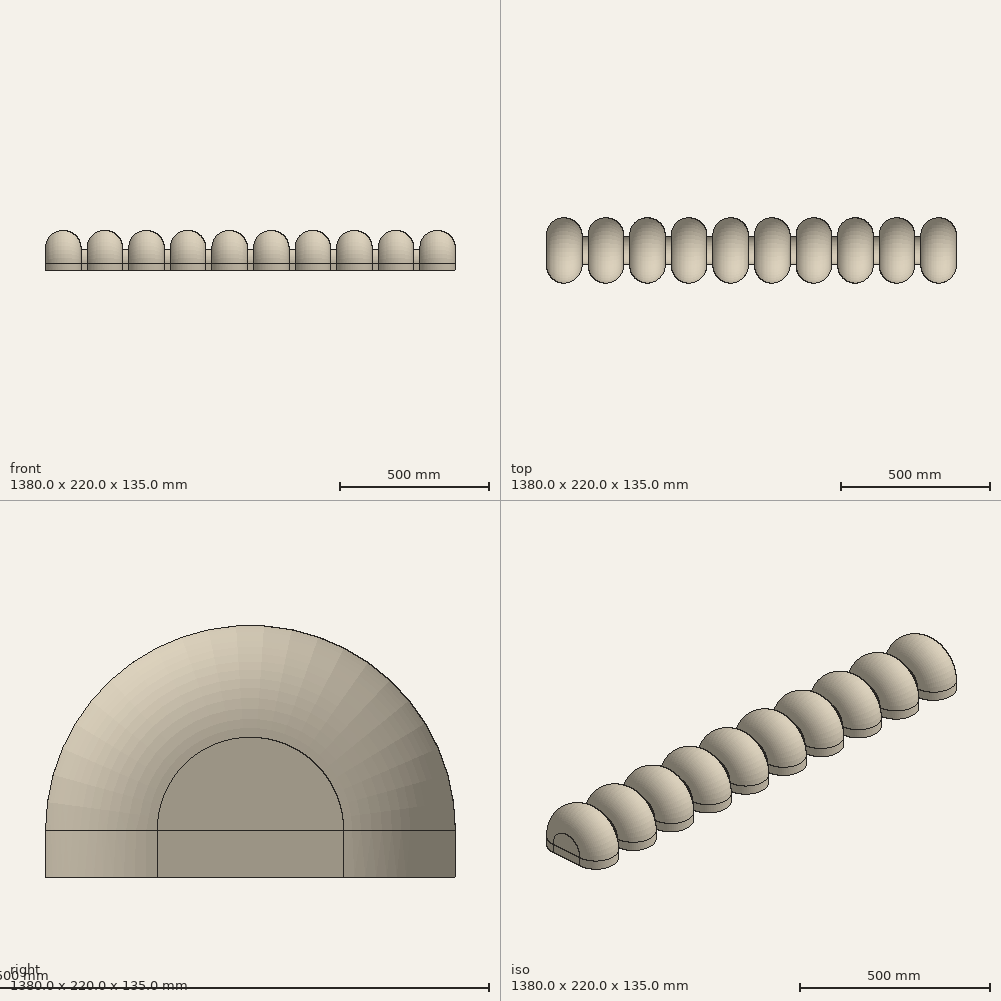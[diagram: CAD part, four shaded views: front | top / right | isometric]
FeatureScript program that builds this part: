
annotation { "Feature Type Name" : "Feature", "Feature Type Description" : "" }
export const myFeature = defineFeature(function(context is Context, id is Id, definition is map)
    precondition{}
    {
        {
            var Q0;
            Q0=qCreatedBy(makeId("Top.planeOp"),FACE);
            var sketch = newSketch(context, id + "F0", { "sketchPlane" : qUnion([Q0])});
            skArc(sketch, "E0", {"start": v(50, 0) * mm, "mid": v(0, 50) * mm, "end": v(-50, 0) * mm});
            skLineSegment(sketch, "E1", {"start": v(-50, 0) * mm, "end": v(-50, -100) * mm});
            skLineSegment(sketch, "E2", {"start": v(50, 0) * mm, "end": v(50, -13) * mm});
            skArc(sketch, "E3", {"start": v(-50, -100) * mm, "mid": v(0, -150) * mm, "end": v(50, -100) * mm});
            skLineSegment(sketch, "E4.bottom", {"start": v(50, -13) * mm, "end": v(90, -13) * mm});
            skLineSegment(sketch, "E4.top", {"start": v(50, -87) * mm, "end": v(90, -87) * mm});
            skLineSegment(sketch, "E5", {"start": v(90, 0) * mm, "end": v(90, -13) * mm});
            skLineSegment(sketch, "E6", {"start": v(190, 0) * mm, "end": v(190, -13) * mm});
            skArc(sketch, "E7", {"start": v(90, 0) * mm, "mid": v(140, 50) * mm, "end": v(190, 0) * mm});
            skArc(sketch, "E8", {"start": v(190, -100) * mm, "mid": v(140, -150) * mm, "end": v(90, -100) * mm});
            skLineSegment(sketch, "E9.trimOffspring", {"start": v(90, -87) * mm, "end": v(90, -100) * mm});
            skLineSegment(sketch, "E10.trimOffspring", {"start": v(50, -87) * mm, "end": v(50, -100) * mm});
            skLineSegment(sketch, "E11.bottom", {"start": v(190, -13) * mm, "end": v(230, -13) * mm});
            skLineSegment(sketch, "E11.top", {"start": v(190, -87) * mm, "end": v(230, -87) * mm});
            skLineSegment(sketch, "E12", {"start": v(230, 0) * mm, "end": v(230, -13) * mm});
            skLineSegment(sketch, "E13", {"start": v(330, -100) * mm, "end": v(330, -87) * mm});
            skArc(sketch, "E14", {"start": v(230, 0) * mm, "mid": v(280, 50) * mm, "end": v(330, 0) * mm});
            skArc(sketch, "E15", {"start": v(330, -100) * mm, "mid": v(280, -150) * mm, "end": v(230, -100) * mm});
            skLineSegment(sketch, "E16.trimOffspring", {"start": v(190, -87) * mm, "end": v(190, -100) * mm});
            skLineSegment(sketch, "E17.trimOffspring", {"start": v(230, -87) * mm, "end": v(230, -100) * mm});
            skLineSegment(sketch, "E18.bottom", {"start": v(330, -13) * mm, "end": v(370, -13) * mm});
            skLineSegment(sketch, "E18.top", {"start": v(330, -87) * mm, "end": v(370, -87) * mm});
            skLineSegment(sketch, "E19", {"start": v(370, 0) * mm, "end": v(370, -13) * mm});
            skLineSegment(sketch, "E20", {"start": v(470, -100) * mm, "end": v(470, -87) * mm});
            skArc(sketch, "E21", {"start": v(370, 0) * mm, "mid": v(420, 50) * mm, "end": v(470, 0) * mm});
            skArc(sketch, "E22", {"start": v(470, -100) * mm, "mid": v(420, -150) * mm, "end": v(370, -100) * mm});
            skLineSegment(sketch, "E23.bottom", {"start": v(470, -13) * mm, "end": v(510, -13) * mm});
            skLineSegment(sketch, "E23.top", {"start": v(470, -87) * mm, "end": v(510, -87) * mm});
            skLineSegment(sketch, "E24", {"start": v(510, 0) * mm, "end": v(510, -13) * mm});
            skLineSegment(sketch, "E25", {"start": v(610, -100) * mm, "end": v(610, -87) * mm});
            skArc(sketch, "E26", {"start": v(510, 0) * mm, "mid": v(560, 50) * mm, "end": v(610, 0) * mm});
            skArc(sketch, "E27", {"start": v(610, -100) * mm, "mid": v(560, -150) * mm, "end": v(510, -100) * mm});
            skLineSegment(sketch, "E28.bottom", {"start": v(610, -13) * mm, "end": v(650, -13) * mm});
            skLineSegment(sketch, "E28.top", {"start": v(610, -87) * mm, "end": v(650, -87) * mm});
            skLineSegment(sketch, "E29", {"start": v(650, 0) * mm, "end": v(650, -13) * mm});
            skLineSegment(sketch, "E30", {"start": v(750, -100) * mm, "end": v(750, -87) * mm});
            skArc(sketch, "E31", {"start": v(650, 0) * mm, "mid": v(700, 50) * mm, "end": v(750, 0) * mm});
            skArc(sketch, "E32", {"start": v(750, -100) * mm, "mid": v(700, -150) * mm, "end": v(650, -100) * mm});
            skLineSegment(sketch, "E33.bottom", {"start": v(750, -13) * mm, "end": v(790, -13) * mm});
            skLineSegment(sketch, "E33.top", {"start": v(750, -87) * mm, "end": v(790, -87) * mm});
            skLineSegment(sketch, "E34", {"start": v(790, 0) * mm, "end": v(790, -13) * mm});
            skLineSegment(sketch, "E35", {"start": v(890, -100) * mm, "end": v(890, -87) * mm});
            skArc(sketch, "E36", {"start": v(790, 0) * mm, "mid": v(840, 50) * mm, "end": v(890, 0) * mm});
            skArc(sketch, "E37", {"start": v(890, -100) * mm, "mid": v(840, -150) * mm, "end": v(790, -100) * mm});
            skLineSegment(sketch, "E38.bottom", {"start": v(890, -13) * mm, "end": v(930, -13) * mm});
            skLineSegment(sketch, "E38.top", {"start": v(890, -87) * mm, "end": v(930, -87) * mm});
            skLineSegment(sketch, "E39", {"start": v(930, 0) * mm, "end": v(930, -13) * mm});
            skLineSegment(sketch, "E40", {"start": v(1030, -100) * mm, "end": v(1030, -87) * mm});
            skArc(sketch, "E41", {"start": v(1030, 0) * mm, "mid": v(980, 50) * mm, "end": v(930, 0) * mm});
            skArc(sketch, "E42", {"start": v(930, -100) * mm, "mid": v(980, -150) * mm, "end": v(1030, -100) * mm});
            skLineSegment(sketch, "E43.bottom", {"start": v(1030, -13) * mm, "end": v(1070, -13) * mm});
            skLineSegment(sketch, "E43.top", {"start": v(1030, -87) * mm, "end": v(1070, -87) * mm});
            skLineSegment(sketch, "E44", {"start": v(1070, 0) * mm, "end": v(1070, -13) * mm});
            skLineSegment(sketch, "E45", {"start": v(1170, -100) * mm, "end": v(1170, -87) * mm});
            skArc(sketch, "E46", {"start": v(1170, 0) * mm, "mid": v(1120, 50) * mm, "end": v(1070, 0) * mm});
            skArc(sketch, "E47", {"start": v(1070, -100) * mm, "mid": v(1120, -150) * mm, "end": v(1170, -100) * mm});
            skLineSegment(sketch, "E48.bottom", {"start": v(1170, -13) * mm, "end": v(1210, -13) * mm});
            skLineSegment(sketch, "E48.top", {"start": v(1170, -87) * mm, "end": v(1210, -87) * mm});
            skLineSegment(sketch, "E49", {"start": v(1210, 0) * mm, "end": v(1210, -13) * mm});
            skLineSegment(sketch, "E50", {"start": v(1310, -100) * mm, "end": v(1310, 0) * mm});
            skArc(sketch, "E51", {"start": v(1310, 0) * mm, "mid": v(1260, 50) * mm, "end": v(1210, 0) * mm});
            skArc(sketch, "E52", {"start": v(1310, -100) * mm, "mid": v(1260, -150) * mm, "end": v(1210, -100) * mm});
            skLineSegment(sketch, "E53.trimOffspring", {"start": v(1170, -13) * mm, "end": v(1170, 0) * mm});
            skLineSegment(sketch, "E54.trimOffspring", {"start": v(1210, -87) * mm, "end": v(1210, -100) * mm});
            skLineSegment(sketch, "E55.trimOffspring", {"start": v(1030, -13) * mm, "end": v(1030, 0) * mm});
            skLineSegment(sketch, "E56.trimOffspring", {"start": v(1070, -87) * mm, "end": v(1070, -100) * mm});
            skLineSegment(sketch, "E57.trimOffspring", {"start": v(930, -87) * mm, "end": v(930, -100) * mm});
            skLineSegment(sketch, "E58.trimOffspring", {"start": v(890, -13) * mm, "end": v(890, 0) * mm});
            skLineSegment(sketch, "E59.trimOffspring", {"start": v(790, -87) * mm, "end": v(790, -100) * mm});
            skLineSegment(sketch, "E60.trimOffspring", {"start": v(750, -13) * mm, "end": v(750, 0) * mm});
            skLineSegment(sketch, "E61.trimOffspring", {"start": v(650, -87) * mm, "end": v(650, -100) * mm});
            skLineSegment(sketch, "E62.trimOffspring", {"start": v(610, -13) * mm, "end": v(610, 0) * mm});
            skLineSegment(sketch, "E63.trimOffspring", {"start": v(510, -87) * mm, "end": v(510, -100) * mm});
            skLineSegment(sketch, "E64.trimOffspring", {"start": v(470, -13) * mm, "end": v(470, 0) * mm});
            skLineSegment(sketch, "E65.trimOffspring", {"start": v(370, -87) * mm, "end": v(370, -100) * mm});
            skLineSegment(sketch, "E66.trimOffspring", {"start": v(330, -13) * mm, "end": v(330, 0) * mm});
            skSolve(sketch);
        }
        {
            var Q0;
            Q0=makeQuery(id+"F0.imprint","IMPRINT",FACE,{"disambiguationData":[TD([[makeQuery(id+"F0.imprint","IMPRINT",EDGE,{"derivedFrom":sQuery(id+"F0.wireOp",EDGE,"E0")}),1.0]])]});
            extrude(context, id + "F1", {"entities" : qUnion([Q0]), "depth" : 25 * mm});
        }
        {
            var Q0;
            Q0=makeQuery(id+"F1.opExtrude","CAP_FACE",FACE,{"disambiguationData":[OSD([sQuery(id+"F0.wireOp",EDGE,"E0"),sQuery(id+"F0.wireOp",EDGE,"E1"),sQuery(id+"F0.wireOp",EDGE,"E2"),sQuery(id+"F0.wireOp",EDGE,"E3"),sQuery(id+"F0.wireOp",EDGE,"E4.bottom"),sQuery(id+"F0.wireOp",EDGE,"E4.top"),sQuery(id+"F0.wireOp",EDGE,"E5"),sQuery(id+"F0.wireOp",EDGE,"E6"),sQuery(id+"F0.wireOp",EDGE,"E7"),sQuery(id+"F0.wireOp",EDGE,"E8"),sQuery(id+"F0.wireOp",EDGE,"E9.trimOffspring"),sQuery(id+"F0.wireOp",EDGE,"E10.trimOffspring"),sQuery(id+"F0.wireOp",EDGE,"E11.bottom"),sQuery(id+"F0.wireOp",EDGE,"E11.top"),sQuery(id+"F0.wireOp",EDGE,"E12"),sQuery(id+"F0.wireOp",EDGE,"E13"),sQuery(id+"F0.wireOp",EDGE,"E14"),sQuery(id+"F0.wireOp",EDGE,"E15"),sQuery(id+"F0.wireOp",EDGE,"E16.trimOffspring"),sQuery(id+"F0.wireOp",EDGE,"E17.trimOffspring"),sQuery(id+"F0.wireOp",EDGE,"E18.bottom"),sQuery(id+"F0.wireOp",EDGE,"E18.top"),sQuery(id+"F0.wireOp",EDGE,"E19"),sQuery(id+"F0.wireOp",EDGE,"E20"),sQuery(id+"F0.wireOp",EDGE,"E21"),sQuery(id+"F0.wireOp",EDGE,"E22"),sQuery(id+"F0.wireOp",EDGE,"E23.bottom"),sQuery(id+"F0.wireOp",EDGE,"E23.top"),sQuery(id+"F0.wireOp",EDGE,"E24"),sQuery(id+"F0.wireOp",EDGE,"E25"),sQuery(id+"F0.wireOp",EDGE,"E26"),sQuery(id+"F0.wireOp",EDGE,"E27"),sQuery(id+"F0.wireOp",EDGE,"E28.bottom"),sQuery(id+"F0.wireOp",EDGE,"E28.top"),sQuery(id+"F0.wireOp",EDGE,"E29"),sQuery(id+"F0.wireOp",EDGE,"E30"),sQuery(id+"F0.wireOp",EDGE,"E31"),sQuery(id+"F0.wireOp",EDGE,"E32"),sQuery(id+"F0.wireOp",EDGE,"E33.bottom"),sQuery(id+"F0.wireOp",EDGE,"E33.top"),sQuery(id+"F0.wireOp",EDGE,"E34"),sQuery(id+"F0.wireOp",EDGE,"E35"),sQuery(id+"F0.wireOp",EDGE,"E36"),sQuery(id+"F0.wireOp",EDGE,"E37"),sQuery(id+"F0.wireOp",EDGE,"E38.bottom"),sQuery(id+"F0.wireOp",EDGE,"E38.top"),sQuery(id+"F0.wireOp",EDGE,"E39"),sQuery(id+"F0.wireOp",EDGE,"E40"),sQuery(id+"F0.wireOp",EDGE,"E41"),sQuery(id+"F0.wireOp",EDGE,"E42"),sQuery(id+"F0.wireOp",EDGE,"E43.bottom"),sQuery(id+"F0.wireOp",EDGE,"E43.top"),sQuery(id+"F0.wireOp",EDGE,"E44"),sQuery(id+"F0.wireOp",EDGE,"E45"),sQuery(id+"F0.wireOp",EDGE,"E46"),sQuery(id+"F0.wireOp",EDGE,"E47"),sQuery(id+"F0.wireOp",EDGE,"E48.bottom"),sQuery(id+"F0.wireOp",EDGE,"E48.top"),sQuery(id+"F0.wireOp",EDGE,"E49"),sQuery(id+"F0.wireOp",EDGE,"E50"),sQuery(id+"F0.wireOp",EDGE,"E51"),sQuery(id+"F0.wireOp",EDGE,"E52"),sQuery(id+"F0.wireOp",EDGE,"E53.trimOffspring"),sQuery(id+"F0.wireOp",EDGE,"E54.trimOffspring"),sQuery(id+"F0.wireOp",EDGE,"E55.trimOffspring"),sQuery(id+"F0.wireOp",EDGE,"E56.trimOffspring"),sQuery(id+"F0.wireOp",EDGE,"E57.trimOffspring"),sQuery(id+"F0.wireOp",EDGE,"E58.trimOffspring"),sQuery(id+"F0.wireOp",EDGE,"E59.trimOffspring"),sQuery(id+"F0.wireOp",EDGE,"E60.trimOffspring"),sQuery(id+"F0.wireOp",EDGE,"E61.trimOffspring"),sQuery(id+"F0.wireOp",EDGE,"E62.trimOffspring"),sQuery(id+"F0.wireOp",EDGE,"E63.trimOffspring"),sQuery(id+"F0.wireOp",EDGE,"E64.trimOffspring"),sQuery(id+"F0.wireOp",EDGE,"E65.trimOffspring"),sQuery(id+"F0.wireOp",EDGE,"E66.trimOffspring")])],"isStart":false});
            var sketch = newSketch(context, id + "F2", { "sketchPlane" : qUnion([Q0])});
            skLineSegment(sketch, "E67", {"start": v(470, 0) * mm, "end": v(470, -13) * mm});
            skLineSegment(sketch, "E68", {"start": v(470, -13) * mm, "end": v(510, -13) * mm});
            skLineSegment(sketch, "E69", {"start": v(510, -13) * mm, "end": v(510, 0) * mm});
            skArc(sketch, "E70", {"start": v(510, 0) * mm, "mid": v(560, 50) * mm, "end": v(610, 0) * mm});
            skLineSegment(sketch, "E71", {"start": v(610, 0) * mm, "end": v(610, -13) * mm});
            skLineSegment(sketch, "E72", {"start": v(610, -13) * mm, "end": v(650, -13) * mm});
            skLineSegment(sketch, "E73", {"start": v(650, -13) * mm, "end": v(650, 0) * mm});
            skArc(sketch, "E74", {"start": v(650, 0) * mm, "mid": v(700, 50) * mm, "end": v(750, 0) * mm});
            skLineSegment(sketch, "E75", {"start": v(750, 0) * mm, "end": v(750, -13) * mm});
            skLineSegment(sketch, "E76", {"start": v(750, -13) * mm, "end": v(790, -13) * mm});
            skLineSegment(sketch, "E77", {"start": v(790, -13) * mm, "end": v(790, 0) * mm});
            skArc(sketch, "E78", {"start": v(790, 0) * mm, "mid": v(840, 50) * mm, "end": v(890, 0) * mm});
            skLineSegment(sketch, "E79", {"start": v(890, 0) * mm, "end": v(890, -13) * mm});
            skLineSegment(sketch, "E80", {"start": v(890, -13) * mm, "end": v(930, -13) * mm});
            skLineSegment(sketch, "E81", {"start": v(930, -13) * mm, "end": v(930, 0) * mm});
            skArc(sketch, "E82", {"start": v(930, 0) * mm, "mid": v(980, 50) * mm, "end": v(1030, 0) * mm});
            skLineSegment(sketch, "E83", {"start": v(1030, 0) * mm, "end": v(1030, -13) * mm});
            skLineSegment(sketch, "E84", {"start": v(1030, -13) * mm, "end": v(1070, -13) * mm});
            skLineSegment(sketch, "E85", {"start": v(1070, -13) * mm, "end": v(1070, 0) * mm});
            skArc(sketch, "E86", {"start": v(1070, 0) * mm, "mid": v(1120, 50) * mm, "end": v(1170, 0) * mm});
            skLineSegment(sketch, "E87", {"start": v(1170, 0) * mm, "end": v(1170, -13) * mm});
            skLineSegment(sketch, "E88", {"start": v(1170, -13) * mm, "end": v(1210, -13) * mm});
            skLineSegment(sketch, "E89", {"start": v(1210, -13) * mm, "end": v(1210, 0) * mm});
            skArc(sketch, "E90", {"start": v(1210, 0) * mm, "mid": v(1260, 50) * mm, "end": v(1310, 0) * mm});
            skLineSegment(sketch, "E91", {"start": v(1310, 0) * mm, "end": v(1310, -50) * mm});
            skLineSegment(sketch, "E92", {"start": v(330, 0) * mm, "end": v(330, -13) * mm});
            skLineSegment(sketch, "E93", {"start": v(330, -13) * mm, "end": v(370, -13) * mm});
            skLineSegment(sketch, "E94", {"start": v(370, -13) * mm, "end": v(370, 0) * mm});
            skArc(sketch, "E95", {"start": v(470, 0) * mm, "mid": v(420, 50) * mm, "end": v(370, 0) * mm});
            skArc(sketch, "E96", {"start": v(330, 0) * mm, "mid": v(280, 50) * mm, "end": v(230, 0) * mm});
            skLineSegment(sketch, "E97", {"start": v(230, 0) * mm, "end": v(230, -13) * mm});
            skLineSegment(sketch, "E98", {"start": v(230, -13) * mm, "end": v(190, -13) * mm});
            skLineSegment(sketch, "E99", {"start": v(190, -13) * mm, "end": v(190, 0) * mm});
            skArc(sketch, "E100", {"start": v(190, 0) * mm, "mid": v(140, 50) * mm, "end": v(90, 0) * mm});
            skLineSegment(sketch, "E101", {"start": v(90, 0) * mm, "end": v(90, -13) * mm});
            skLineSegment(sketch, "E102", {"start": v(90, -13) * mm, "end": v(50, -13) * mm});
            skLineSegment(sketch, "E103", {"start": v(50, -13) * mm, "end": v(50, 0) * mm});
            skArc(sketch, "E104", {"start": v(50, 0) * mm, "mid": v(0, 50) * mm, "end": v(-50, 0) * mm});
            skLineSegment(sketch, "E105", {"start": v(-50, 0) * mm, "end": v(-50, -50) * mm});
            skLineSegment(sketch, "E106.0", {"start": v(1320, 0) * mm, "end": v(1320, -50) * mm});
            skArc(sketch, "E106.1", {"start": v(1200, 0) * mm, "mid": v(1260, 60) * mm, "end": v(1320, 0) * mm});
            skLineSegment(sketch, "E106.2", {"start": v(1200, -3) * mm, "end": v(1200, 0) * mm});
            skLineSegment(sketch, "E106.3", {"start": v(1180, -3) * mm, "end": v(1200, -3) * mm});
            skLineSegment(sketch, "E106.4", {"start": v(1180, 0) * mm, "end": v(1180, -3) * mm});
            skArc(sketch, "E106.5", {"start": v(1060, 0) * mm, "mid": v(1120, 60) * mm, "end": v(1180, 0) * mm});
            skLineSegment(sketch, "E106.6", {"start": v(1060, -3) * mm, "end": v(1060, 0) * mm});
            skLineSegment(sketch, "E106.7", {"start": v(1040, -3) * mm, "end": v(1060, -3) * mm});
            skLineSegment(sketch, "E106.8", {"start": v(1040, 0) * mm, "end": v(1040, -3) * mm});
            skArc(sketch, "E106.9", {"start": v(920, 0) * mm, "mid": v(980, 60) * mm, "end": v(1040, 0) * mm});
            skLineSegment(sketch, "E106.10", {"start": v(920, -3) * mm, "end": v(920, 0) * mm});
            skLineSegment(sketch, "E106.11", {"start": v(900, -3) * mm, "end": v(920, -3) * mm});
            skLineSegment(sketch, "E106.12", {"start": v(900, 0) * mm, "end": v(900, -3) * mm});
            skArc(sketch, "E106.13", {"start": v(780, 0) * mm, "mid": v(840, 60) * mm, "end": v(900, 0) * mm});
            skLineSegment(sketch, "E106.14", {"start": v(780, -3) * mm, "end": v(780, 0) * mm});
            skLineSegment(sketch, "E106.15", {"start": v(760, -3) * mm, "end": v(780, -3) * mm});
            skLineSegment(sketch, "E106.16", {"start": v(760, 0) * mm, "end": v(760, -3) * mm});
            skArc(sketch, "E106.17", {"start": v(340, 0) * mm, "mid": v(280, 60) * mm, "end": v(220, 0) * mm});
            skLineSegment(sketch, "E106.18", {"start": v(220, 0) * mm, "end": v(220, -3) * mm});
            skLineSegment(sketch, "E106.19", {"start": v(220, -3) * mm, "end": v(200, -3) * mm});
            skLineSegment(sketch, "E106.20", {"start": v(200, -3) * mm, "end": v(200, 0) * mm});
            skArc(sketch, "E106.21", {"start": v(200, 0) * mm, "mid": v(140, 60) * mm, "end": v(80, 0) * mm});
            skLineSegment(sketch, "E106.22", {"start": v(80, 0) * mm, "end": v(80, -3) * mm});
            skLineSegment(sketch, "E106.23", {"start": v(-60, 0) * mm, "end": v(-60, -50) * mm});
            skArc(sketch, "E106.24", {"start": v(60, 0) * mm, "mid": v(0, 60) * mm, "end": v(-60, 0) * mm});
            skLineSegment(sketch, "E106.25", {"start": v(60, -3) * mm, "end": v(60, 0) * mm});
            skLineSegment(sketch, "E106.26", {"start": v(80, -3) * mm, "end": v(60, -3) * mm});
            skLineSegment(sketch, "E106.27", {"start": v(340, 0) * mm, "end": v(340, -3) * mm});
            skLineSegment(sketch, "E106.28", {"start": v(340, -3) * mm, "end": v(360, -3) * mm});
            skLineSegment(sketch, "E106.29", {"start": v(360, -3) * mm, "end": v(360, 0) * mm});
            skArc(sketch, "E106.30", {"start": v(480, 0) * mm, "mid": v(420, 60) * mm, "end": v(360, 0) * mm});
            skLineSegment(sketch, "E106.31", {"start": v(480, 0) * mm, "end": v(480, -3) * mm});
            skLineSegment(sketch, "E106.32", {"start": v(480, -3) * mm, "end": v(500, -3) * mm});
            skLineSegment(sketch, "E106.33", {"start": v(500, -3) * mm, "end": v(500, 0) * mm});
            skArc(sketch, "E106.34", {"start": v(500, 0) * mm, "mid": v(560, 60) * mm, "end": v(620, 0) * mm});
            skLineSegment(sketch, "E106.35", {"start": v(620, 0) * mm, "end": v(620, -3) * mm});
            skLineSegment(sketch, "E106.36", {"start": v(620, -3) * mm, "end": v(640, -3) * mm});
            skLineSegment(sketch, "E106.37", {"start": v(640, -3) * mm, "end": v(640, 0) * mm});
            skArc(sketch, "E106.38", {"start": v(640, 0) * mm, "mid": v(700, 60) * mm, "end": v(760, 0) * mm});
            skLineSegment(sketch, "E107", {"start": v(-60, -50) * mm, "end": v(-50, -50) * mm});
            skLineSegment(sketch, "E108", {"start": v(1320, -50) * mm, "end": v(1310, -50) * mm});
            skLineSegment(sketch, "E109", {"start": v(-60, -50) * mm, "end": v(1320, -50) * mm});
            skSolve(sketch);
        }
        {
            var Q0;
            Q0=qCreatedBy(makeId("Top.planeOp"),FACE);
            var sketch = newSketch(context, id + "F3", { "sketchPlane" : qUnion([Q0])});
            skLineSegment(sketch, "E110", {"start": v(-50, -100) * mm, "end": v(-50, 0) * mm});
            skArc(sketch, "E111", {"start": v(-50, 0) * mm, "mid": v(0, 50) * mm, "end": v(50, 0) * mm});
            skLineSegment(sketch, "E112", {"start": v(50, 0) * mm, "end": v(50, -13) * mm});
            skLineSegment(sketch, "E113", {"start": v(50, -13) * mm, "end": v(90, -13) * mm});
            skLineSegment(sketch, "E114", {"start": v(90, -13) * mm, "end": v(90, 0) * mm});
            skArc(sketch, "E115", {"start": v(90, 0) * mm, "mid": v(140, 50) * mm, "end": v(190, 0) * mm});
            skLineSegment(sketch, "E116", {"start": v(190, 0) * mm, "end": v(190, -13) * mm});
            skLineSegment(sketch, "E117", {"start": v(190, -13) * mm, "end": v(230, -13) * mm});
            skLineSegment(sketch, "E118", {"start": v(230, -13) * mm, "end": v(230, 0) * mm});
            skArc(sketch, "E119", {"start": v(230, 0) * mm, "mid": v(280, 50) * mm, "end": v(330, 0) * mm});
            skLineSegment(sketch, "E120", {"start": v(330, 0) * mm, "end": v(330, -13) * mm});
            skLineSegment(sketch, "E121", {"start": v(330, -13) * mm, "end": v(370, -13) * mm});
            skLineSegment(sketch, "E122", {"start": v(370, -13) * mm, "end": v(370, 0) * mm});
            skArc(sketch, "E123", {"start": v(370, 0) * mm, "mid": v(420, 50) * mm, "end": v(470, 0) * mm});
            skLineSegment(sketch, "E124", {"start": v(470, 0) * mm, "end": v(470, -13) * mm});
            skLineSegment(sketch, "E125", {"start": v(470, -13) * mm, "end": v(510, -13) * mm});
            skLineSegment(sketch, "E126", {"start": v(510, -13) * mm, "end": v(510, 0) * mm});
            skArc(sketch, "E127", {"start": v(510, 0) * mm, "mid": v(560, 50) * mm, "end": v(610, 0) * mm});
            skLineSegment(sketch, "E128", {"start": v(610, 0) * mm, "end": v(610, -13) * mm});
            skLineSegment(sketch, "E129", {"start": v(610, -13) * mm, "end": v(650, -13) * mm});
            skLineSegment(sketch, "E130", {"start": v(650, -13) * mm, "end": v(650, 0) * mm});
            skArc(sketch, "E131", {"start": v(650, 0) * mm, "mid": v(700, 50) * mm, "end": v(750, 0) * mm});
            skLineSegment(sketch, "E132", {"start": v(750, 0) * mm, "end": v(750, -13) * mm});
            skLineSegment(sketch, "E133", {"start": v(750, -13) * mm, "end": v(790, -13) * mm});
            skLineSegment(sketch, "E134", {"start": v(790, -13) * mm, "end": v(790, 0) * mm});
            skArc(sketch, "E135", {"start": v(790, 0) * mm, "mid": v(840, 50) * mm, "end": v(890, 0) * mm});
            skLineSegment(sketch, "E136", {"start": v(890, 0) * mm, "end": v(890, -13) * mm});
            skLineSegment(sketch, "E137", {"start": v(890, -13) * mm, "end": v(930, -13) * mm});
            skLineSegment(sketch, "E138", {"start": v(930, -13) * mm, "end": v(930, 0) * mm});
            skArc(sketch, "E139", {"start": v(930, 0) * mm, "mid": v(980, 50) * mm, "end": v(1030, 0) * mm});
            skLineSegment(sketch, "E140", {"start": v(1030, 0) * mm, "end": v(1030, -13) * mm});
            skLineSegment(sketch, "E141", {"start": v(1030, -13) * mm, "end": v(1070, -13) * mm});
            skLineSegment(sketch, "E142", {"start": v(1070, -13) * mm, "end": v(1070, 0) * mm});
            skArc(sketch, "E143", {"start": v(1070, 0) * mm, "mid": v(1120, 50) * mm, "end": v(1170, 0) * mm});
            skLineSegment(sketch, "E144", {"start": v(1170, 0) * mm, "end": v(1170, -13) * mm});
            skLineSegment(sketch, "E145", {"start": v(1170, -13) * mm, "end": v(1210, -13) * mm});
            skLineSegment(sketch, "E146", {"start": v(1210, -13) * mm, "end": v(1210, 0) * mm});
            skArc(sketch, "E147", {"start": v(1210, 0) * mm, "mid": v(1260, 50) * mm, "end": v(1310, 0) * mm});
            skLineSegment(sketch, "E148", {"start": v(1310, 0) * mm, "end": v(1310, -100) * mm});
            skArc(sketch, "E149", {"start": v(1310, -100) * mm, "mid": v(1260, -150) * mm, "end": v(1210, -100) * mm});
            skLineSegment(sketch, "E150", {"start": v(1210, -100) * mm, "end": v(1210, -87) * mm});
            skLineSegment(sketch, "E151", {"start": v(1210, -87) * mm, "end": v(1170, -87) * mm});
            skLineSegment(sketch, "E152", {"start": v(1170, -87) * mm, "end": v(1170, -100) * mm});
            skArc(sketch, "E153", {"start": v(1170, -100) * mm, "mid": v(1120, -150) * mm, "end": v(1070, -100) * mm});
            skLineSegment(sketch, "E154", {"start": v(1070, -100) * mm, "end": v(1070, -87) * mm});
            skLineSegment(sketch, "E155", {"start": v(1070, -87) * mm, "end": v(1030, -87) * mm});
            skLineSegment(sketch, "E156", {"start": v(1030, -87) * mm, "end": v(1030, -100) * mm});
            skArc(sketch, "E157", {"start": v(1030, -100) * mm, "mid": v(980, -150) * mm, "end": v(930, -100) * mm});
            skLineSegment(sketch, "E158", {"start": v(930, -100) * mm, "end": v(930, -87) * mm});
            skLineSegment(sketch, "E159", {"start": v(930, -87) * mm, "end": v(890, -87) * mm});
            skLineSegment(sketch, "E160", {"start": v(890, -87) * mm, "end": v(890, -100) * mm});
            skArc(sketch, "E161", {"start": v(890, -100) * mm, "mid": v(840, -150) * mm, "end": v(790, -100) * mm});
            skLineSegment(sketch, "E162", {"start": v(790, -100) * mm, "end": v(790, -87) * mm});
            skLineSegment(sketch, "E163", {"start": v(790, -87) * mm, "end": v(750, -87) * mm});
            skLineSegment(sketch, "E164", {"start": v(750, -87) * mm, "end": v(750, -100) * mm});
            skArc(sketch, "E165", {"start": v(750, -100) * mm, "mid": v(700, -150) * mm, "end": v(650, -100) * mm});
            skLineSegment(sketch, "E166", {"start": v(650, -100) * mm, "end": v(650, -87) * mm});
            skLineSegment(sketch, "E167", {"start": v(650, -87) * mm, "end": v(610, -87) * mm});
            skLineSegment(sketch, "E168", {"start": v(610, -87) * mm, "end": v(610, -100) * mm});
            skArc(sketch, "E169", {"start": v(610, -100) * mm, "mid": v(560, -150) * mm, "end": v(510, -100) * mm});
            skLineSegment(sketch, "E170", {"start": v(510, -100) * mm, "end": v(510, -87) * mm});
            skLineSegment(sketch, "E171", {"start": v(510, -87) * mm, "end": v(470, -87) * mm});
            skLineSegment(sketch, "E172", {"start": v(470, -87) * mm, "end": v(470, -100) * mm});
            skArc(sketch, "E173", {"start": v(470, -100) * mm, "mid": v(420, -150) * mm, "end": v(370, -100) * mm});
            skLineSegment(sketch, "E174", {"start": v(370, -100) * mm, "end": v(370, -87) * mm});
            skLineSegment(sketch, "E175", {"start": v(370, -87) * mm, "end": v(330, -87) * mm});
            skLineSegment(sketch, "E176", {"start": v(330, -87) * mm, "end": v(330, -100) * mm});
            skArc(sketch, "E177", {"start": v(330, -100) * mm, "mid": v(280, -150) * mm, "end": v(230, -100) * mm});
            skLineSegment(sketch, "E178", {"start": v(230, -100) * mm, "end": v(230, -87) * mm});
            skLineSegment(sketch, "E179", {"start": v(230, -87) * mm, "end": v(190, -87) * mm});
            skLineSegment(sketch, "E180", {"start": v(190, -87) * mm, "end": v(190, -100) * mm});
            skArc(sketch, "E181", {"start": v(190, -100) * mm, "mid": v(140, -150) * mm, "end": v(90, -100) * mm});
            skLineSegment(sketch, "E182", {"start": v(90, -100) * mm, "end": v(90, -87) * mm});
            skLineSegment(sketch, "E183", {"start": v(90, -87) * mm, "end": v(50, -87) * mm});
            skLineSegment(sketch, "E184", {"start": v(50, -87) * mm, "end": v(50, -100) * mm});
            skArc(sketch, "E185", {"start": v(50, -100) * mm, "mid": v(0, -150) * mm, "end": v(-50, -100) * mm});
            skLineSegment(sketch, "E186.0", {"start": v(80.08, -97) * mm, "end": v(59.93, -97) * mm});
            skArc(sketch, "E186.1", {"start": v(199.93, -97) * mm, "mid": v(140, -160) * mm, "end": v(80.08, -97) * mm});
            skLineSegment(sketch, "E186.2", {"start": v(220.08, -97) * mm, "end": v(199.93, -97) * mm});
            skArc(sketch, "E186.3", {"start": v(339.93, -97) * mm, "mid": v(280, -160) * mm, "end": v(220.08, -97) * mm});
            skLineSegment(sketch, "E186.4", {"start": v(360.08, -97) * mm, "end": v(339.93, -97) * mm});
            skArc(sketch, "E186.5", {"start": v(479.93, -97) * mm, "mid": v(420, -160) * mm, "end": v(360.08, -97) * mm});
            skLineSegment(sketch, "E186.6", {"start": v(500.08, -97) * mm, "end": v(479.93, -97) * mm});
            skArc(sketch, "E186.7", {"start": v(619.93, -97) * mm, "mid": v(560, -160) * mm, "end": v(500.08, -97) * mm});
            skLineSegment(sketch, "E186.8", {"start": v(640.08, -97) * mm, "end": v(619.93, -97) * mm});
            skArc(sketch, "E186.9", {"start": v(759.93, -97) * mm, "mid": v(700, -160) * mm, "end": v(640.08, -97) * mm});
            skLineSegment(sketch, "E186.10", {"start": v(780.08, -97) * mm, "end": v(759.93, -97) * mm});
            skArc(sketch, "E186.11", {"start": v(59.93, -97) * mm, "mid": v(1.5, -159.98) * mm, "end": v(-60, -100) * mm});
            skArc(sketch, "E186.12", {"start": v(899.93, -97) * mm, "mid": v(840, -160) * mm, "end": v(780.08, -97) * mm});
            skLineSegment(sketch, "E186.13", {"start": v(920.08, -97) * mm, "end": v(899.93, -97) * mm});
            skArc(sketch, "E186.14", {"start": v(1039.93, -97) * mm, "mid": v(980, -160) * mm, "end": v(920.08, -97) * mm});
            skLineSegment(sketch, "E186.15", {"start": v(1060.08, -97) * mm, "end": v(1039.93, -97) * mm});
            skArc(sketch, "E186.16", {"start": v(1179.93, -97) * mm, "mid": v(1120, -160) * mm, "end": v(1060.08, -97) * mm});
            skLineSegment(sketch, "E186.17", {"start": v(1200.08, -97) * mm, "end": v(1179.93, -97) * mm});
            skArc(sketch, "E186.18", {"start": v(500.08, -3) * mm, "mid": v(560, 60) * mm, "end": v(619.93, -3) * mm});
            skLineSegment(sketch, "E186.19", {"start": v(479.93, -3) * mm, "end": v(500.08, -3) * mm});
            skArc(sketch, "E186.20", {"start": v(360.08, -3) * mm, "mid": v(420, 60) * mm, "end": v(479.93, -3) * mm});
            skLineSegment(sketch, "E186.21", {"start": v(339.93, -3) * mm, "end": v(360.08, -3) * mm});
            skArc(sketch, "E186.22", {"start": v(220.08, -3) * mm, "mid": v(280, 60) * mm, "end": v(339.93, -3) * mm});
            skLineSegment(sketch, "E186.23", {"start": v(199.93, -3) * mm, "end": v(220.08, -3) * mm});
            skLineSegment(sketch, "E186.24", {"start": v(-60, -100) * mm, "end": v(-60, 0) * mm});
            skArc(sketch, "E186.25", {"start": v(-60, 0) * mm, "mid": v(1.5, 59.98) * mm, "end": v(59.93, -3) * mm});
            skLineSegment(sketch, "E186.26", {"start": v(59.93, -3) * mm, "end": v(80.08, -3) * mm});
            skArc(sketch, "E186.27", {"start": v(80.08, -3) * mm, "mid": v(140, 60) * mm, "end": v(199.93, -3) * mm});
            skLineSegment(sketch, "E186.28", {"start": v(619.93, -3) * mm, "end": v(640.08, -3) * mm});
            skArc(sketch, "E186.29", {"start": v(640.08, -3) * mm, "mid": v(700, 60) * mm, "end": v(759.93, -3) * mm});
            skLineSegment(sketch, "E186.30", {"start": v(759.93, -3) * mm, "end": v(780.08, -3) * mm});
            skArc(sketch, "E186.31", {"start": v(780.08, -3) * mm, "mid": v(840, 60) * mm, "end": v(899.93, -3) * mm});
            skLineSegment(sketch, "E186.32", {"start": v(899.93, -3) * mm, "end": v(920.08, -3) * mm});
            skArc(sketch, "E186.33", {"start": v(920.08, -3) * mm, "mid": v(980, 60) * mm, "end": v(1039.93, -3) * mm});
            skLineSegment(sketch, "E186.34", {"start": v(1039.93, -3) * mm, "end": v(1060.08, -3) * mm});
            skArc(sketch, "E186.35", {"start": v(1060.08, -3) * mm, "mid": v(1120, 60) * mm, "end": v(1179.93, -3) * mm});
            skLineSegment(sketch, "E186.36", {"start": v(1179.93, -3) * mm, "end": v(1200.08, -3) * mm});
            skArc(sketch, "E186.37", {"start": v(1200.08, -3) * mm, "mid": v(1258.5, 59.98) * mm, "end": v(1320, 0) * mm});
            skLineSegment(sketch, "E186.38", {"start": v(1320, 0) * mm, "end": v(1320, -100) * mm});
            skArc(sketch, "E186.39", {"start": v(1320, -100) * mm, "mid": v(1258.5, -159.98) * mm, "end": v(1200.08, -97) * mm});
            skSolve(sketch);
        }
        {
            var Q0;
            Q0 = qSketchRegion(id + "F3", true);
            extrude(context, id + "F4", {"entities" : qUnion([Q0]), "operationType" : NewBodyOperationType.ADD, "depth" : 25 * mm});
        }
        {
            var Q0;
            Q0 = qSketchRegion(id + "F2", true);
            var Q1;
            Q1=sQuery(id+"F2.wireOp",EDGE,"E109");
            revolve(context, id + "F5", {"operationType" : NewBodyOperationType.ADD, "entities" : qUnion([Q0]), "axis" : qUnion([Q1]), "revolveType" : RevolveType.ONE_DIRECTION, "angle" : 180 * degree});
        }
    });
